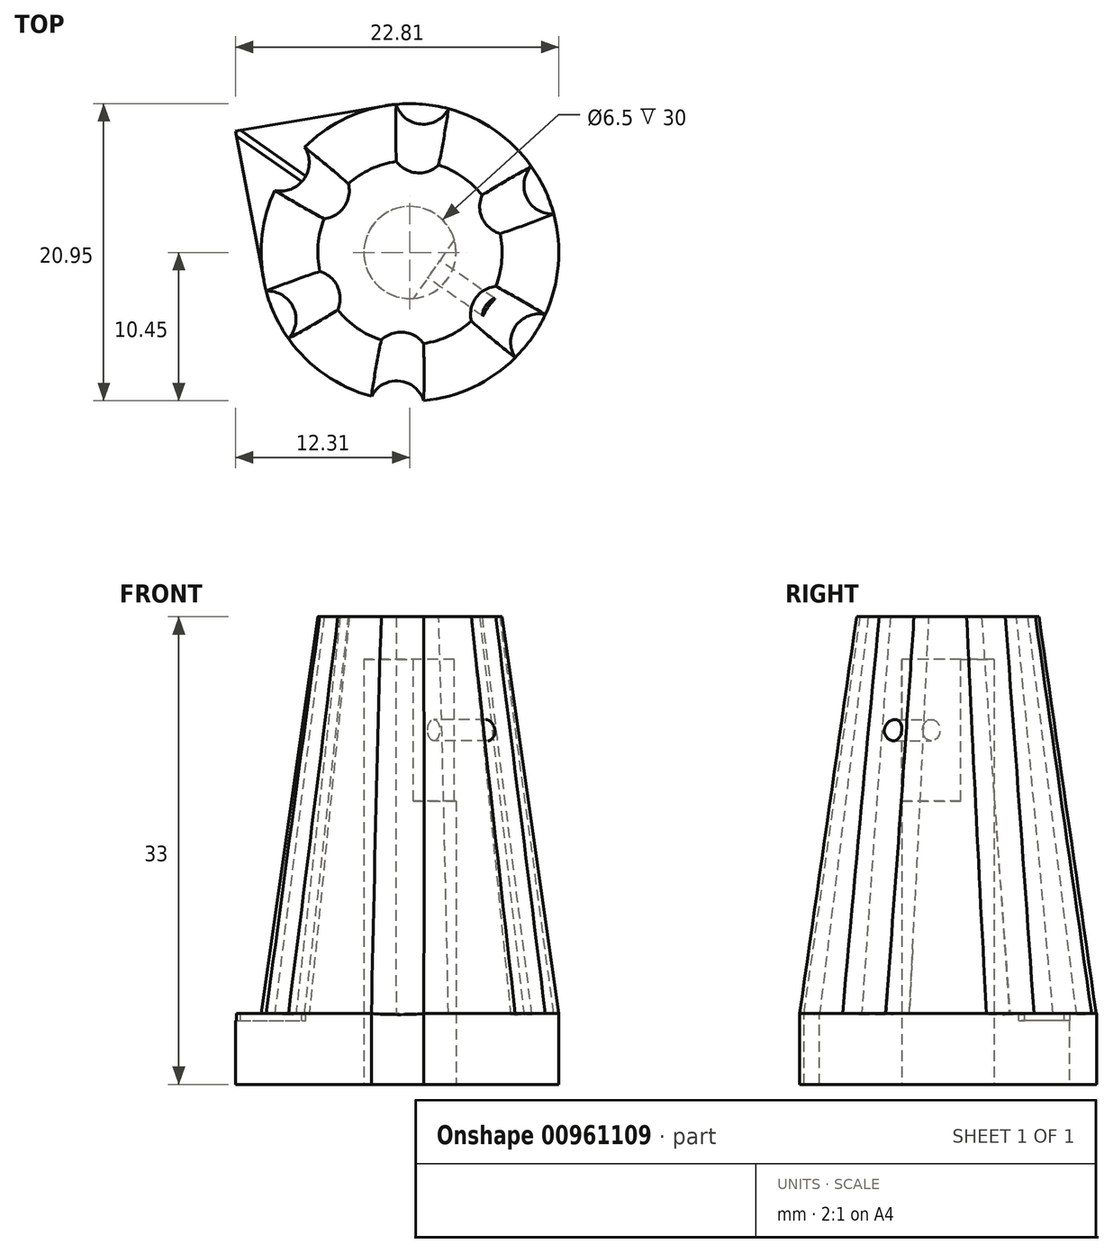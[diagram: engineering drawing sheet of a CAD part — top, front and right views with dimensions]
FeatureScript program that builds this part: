
annotation { "Feature Type Name" : "Feature", "Feature Type Description" : "" }
export const myFeature = defineFeature(function(context is Context, id is Id, definition is map)
    precondition{}
    {
        {
            var Q0;
            Q0=qCreatedBy(makeId("Top.planeOp"),FACE);
            var sketch = newSketch(context, id + "F0", { "sketchPlane" : qUnion([Q0])});
            skCircle(sketch, "E0", {"center": v(0, 0) * mm, "radius": 10.5 * mm});
            skCircle(sketch, "E1", {"center": v(0, 0) * mm, "radius": 3.25 * mm});
            skSolve(sketch);
        }
        {
            var Q0;
            Q0 = qSketchRegion(id + "F0", true);
            var Q1;
            Q1=makeQuery(id+"F0.imprint","IMPRINT",FACE,{"disambiguationData":[TD([[makeQuery(id+"F0.imprint","IMPRINT",EDGE,{"derivedFrom":sQuery(id+"F0.wireOp",EDGE,"E1")}),1.0]])]});
            extrude(context, id + "F1", {"entities" : qUnion([Q0, Q1]), "depth" : 33 * mm, "offsetDistance" : 25 * mm});
        }
        {
            var Q0;
            Q0=makeQuery(id+"F1.opExtrude","CAP_EDGE",EDGE,{"disambiguationData":[OSD([sQuery(id+"F0.wireOp",EDGE,"E0")])],"isStart":false});
            chamfer(context, id + "F2", {"entities" : qUnion([Q0]), "chamferType" : ChamferType.TWO_OFFSETS, "width1" : 4 * mm, "oppositeDirection" : false, "width2" : 28 * mm});
        }
        {
            var Q0;
            Q0=makeQuery(id+"F0.imprint","IMPRINT",FACE,{"disambiguationData":[TD([[makeQuery(id+"F0.imprint","IMPRINT",EDGE,{"derivedFrom":sQuery(id+"F0.wireOp",EDGE,"E1")}),1.0]])]});
            var Q1;
            Q1=sQuery(id+"F0.wireOp",EDGE,"E1");
            extrude(context, id + "F3", {"entities" : qUnion([Q0]), "operationType" : NewBodyOperationType.REMOVE, "surfaceEntities" : qUnion([Q1]), "depth" : 30 * mm, "offsetDistance" : 25 * mm});
        }
        {
            var Q0;
            Q0=qCreatedBy(makeId("Top.planeOp"),FACE);
            cPlane(context, id + "F4", {"entities" : qUnion([Q0]), "cplaneType" : CPlaneType.OFFSET, "offset" : 5 * mm, "width" : 150 * mm, "height" : 150 * mm});
        }
        {
            var Q0;
            Q0=qCreatedBy(id+"F4.planeOp",FACE);
            var sketch = newSketch(context, id + "F5", { "sketchPlane" : qUnion([Q0])});
            skArc(sketch, "E2", {"start": v(0.98, -10.45) * mm, "mid": v(-0.76, -9.06) * mm, "end": v(-2.71, -10.14) * mm});
            skArc(sketch, "E3", {"start": v(-2.71, -10.14) * mm, "mid": v(-0.88, -10.46) * mm, "end": v(0.98, -10.45) * mm});
            skLineSegment(sketch, "E4", {"start": v(-2.71, -10.14) * mm, "end": v(0.98, -10.45) * mm, "construction": true});
            skSolve(sketch);
        }
        {
            var Q0;
            Q0 = qSketchRegion(id + "F5", true);
            extrude(context, id + "F6", {"entities" : qUnion([Q0]), "endBound" : BoundingType.SYMMETRIC, "depth" : 60 * mm, "offsetDistance" : 25 * mm});
        }
        {
            var Q0;
            Q0=makeQuery(id+"F6.opExtrude","SWEPT_BODY",BODY,{"disambiguationData":[OSD([sQuery(id+"F5.wireOp",EDGE,"E2"),sQuery(id+"F5.wireOp",EDGE,"E3")])]});
            var Q1;
            Q1=sQuery(id+"F5.wireOp",EDGE,"E4");
            transform(context, id + "F7", {"entities" : qUnion([Q0]), "transformType" : TransformType.ROTATION, "transformAxis" : qUnion([Q1]), "angle" : 7 * degree, "oppositeDirection" : true, "makeCopy" : false});
        }
        {
            var Q0;
            Q0 = qSketchRegion(id + "F5", true);
            extrude(context, id + "F8", {"entities" : qUnion([Q0]), "operationType" : NewBodyOperationType.REMOVE, "oppositeDirection" : true, "depth" : 25 * mm, "offsetDistance" : 25 * mm});
        }
        {
            var Q0;
            Q0=makeQuery(id+"F6.opExtrude","SWEPT_BODY",BODY,{"disambiguationData":[OSD([sQuery(id+"F5.wireOp",EDGE,"E2"),sQuery(id+"F5.wireOp",EDGE,"E3")])]});
            var Q1;
            Q1=makeQuery(id+"F2.opChamfer","BLEND_FACE",FACE,{"disambiguationData":[OSD([sQuery(id+"F0.wireOp",EDGE,"E0")])]});
            circularPattern(context, id + "F9", {"operationType" : NewBodyOperationType.REMOVE, "entities" : qUnion([Q0]), "axis" : qUnion([Q1]), "angle" : 360 * degree, "instanceCount" : 6, "equalSpace" : true});
        }
        {
            var Q0;
            Q0=makeQuery(id+"F0.imprint","IMPRINT",FACE,{"disambiguationData":[TD([[makeQuery(id+"F0.imprint","IMPRINT",EDGE,{"derivedFrom":sQuery(id+"F0.wireOp",EDGE,"E0")}),1.0]])]});
            var sketch = newSketch(context, id + "F10", { "sketchPlane" : qUnion([Q0])});
            skLineSegment(sketch, "E5", {"start": v(-12.31, 8.57) * mm, "end": v(-10.32, -1.96) * mm});
            skLineSegment(sketch, "E6", {"start": v(-12.31, 8.57) * mm, "end": v(-1.75, 10.35) * mm});
            skLineSegment(sketch, "E7", {"start": v(0, 0) * mm, "end": v(-12.31, 8.57) * mm, "construction": true});
            skSolve(sketch);
        }
        {
            var Q0;
            Q0 = qSketchRegion(id + "F10", true);
            var Q1;
            {var subQ0=sQuery(id+"F10.wireOp",EDGE,"E5");Q1=makeQuery(id+"F10.imprint","IMPRINT",FACE,{"disambiguationData":[TD([[makeQuery(id+"F10.imprint","IMPRINT",EDGE,{"derivedFrom":subQ0}),1.0]])]});}
            extrude(context, id + "F11", {"entities" : qUnion([Q0, Q1]), "operationType" : NewBodyOperationType.ADD, "depth" : 5 * mm, "offsetDistance" : 25 * mm});
        }
        {
            var Q0;
            Q0=makeQuery(id+"F11.opExtrude","CAP_FACE",FACE,{"disambiguationData":[OSD([sQuery(id+"F0.wireOp",EDGE,"E0"),sQuery(id+"F10.wireOp",EDGE,"E5"),sQuery(id+"F10.wireOp",EDGE,"E6"),sQuery(id+"F10.wireOp",EDGE,"PTIv0W1z-BJXX-ulv2-YcXK-IeR1GZzofkEr")])],"isStart":false});
            var sketch = newSketch(context, id + "F12", { "sketchPlane" : qUnion([Q0])});
            skLineSegment(sketch, "E8", {"start": v(-12.31, 8.57) * mm, "end": v(0, 0) * mm, "construction": true});
            skLineSegment(sketch, "E9", {"start": v(-11.96, 8.63) * mm, "end": v(-7.33, 5.4) * mm});
            skLineSegment(sketch, "E10", {"start": v(-12.25, 8.22) * mm, "end": v(-7.62, 5) * mm});
            skSolve(sketch);
        }
        {
            var Q0;
            {var subQ4=sQuery(id+"F12.wireOp",EDGE,"E9");Q0=makeQuery(id+"F12.imprint","IMPRINT",FACE,{"disambiguationData":[TD([[makeQuery(id+"F12.imprint","IMPRINT",EDGE,{"derivedFrom":subQ4}),-1.0]])]});}
            extrude(context, id + "F13", {"entities" : qUnion([Q0]), "operationType" : NewBodyOperationType.REMOVE, "endBound" : BoundingType.SYMMETRIC, "oppositeDirection" : true, "depth" : 1 * mm, "offsetDistance" : 25 * mm});
        }
        {
            var Q0;
            Q0=makeQuery(id+"F3.boolean.opBoolean","COPY",FACE,{"derivedFrom":makeQuery(id+"F3.opExtrude","CAP_FACE",FACE,{"disambiguationData":[OSD([sQuery(id+"F0.wireOp",EDGE,"E1")])],"isStart":false})});
            var sketch = newSketch(context, id + "F14", { "sketchPlane" : qUnion([Q0])});
            skLineSegment(sketch, "E11", {"start": v(0, 0) * mm, "end": v(2.67, 1.86) * mm, "construction": true});
            skLineSegment(sketch, "E12", {"start": v(3.12, -0.9) * mm, "end": v(0.24, 3.24) * mm});
            skSolve(sketch);
        }
        {
            var Q0;
            {var subQ0=sQuery(id+"F14.wireOp",EDGE,"E12");Q0=makeQuery(id+"F14.imprint","IMPRINT",FACE,{"disambiguationData":[TD([[makeQuery(id+"F14.imprint","IMPRINT",EDGE,{"derivedFrom":subQ0}),-1.0]])]});}
            extrude(context, id + "F15", {"entities" : qUnion([Q0]), "operationType" : NewBodyOperationType.ADD, "depth" : 10 * mm, "offsetDistance" : 25 * mm});
        }
        {
            var Q0;
            Q0=makeQuery(id+"F15.opExtrude","SWEPT_FACE",FACE,{"disambiguationData":[OSD([sQuery(id+"F14.wireOp",EDGE,"E12")])]});
            var sketch = newSketch(context, id + "F16", { "sketchPlane" : qUnion([Q0])});
            skCircle(sketch, "E13", {"center": v(0, 25) * mm, "radius": 0.75 * mm});
            skLineSegment(sketch, "E14.bottom", {"start": v(-2.52, 30) * mm, "end": v(2.52, 30) * mm, "construction": true});
            skLineSegment(sketch, "E14.top", {"start": v(-2.52, 20) * mm, "end": v(2.52, 20) * mm, "construction": true});
            skLineSegment(sketch, "E14.left", {"start": v(-2.52, 30) * mm, "end": v(-2.52, 20) * mm, "construction": true});
            skLineSegment(sketch, "E14.right", {"start": v(2.52, 30) * mm, "end": v(2.52, 20) * mm, "construction": true});
            skLineSegment(sketch, "E15", {"start": v(0, 30) * mm, "end": v(0, 20) * mm, "construction": true});
            skSolve(sketch);
        }
        {
            var Q0;
            Q0 = qSketchRegion(id + "F16", true);
            extrude(context, id + "F17", {"entities" : qUnion([Q0]), "operationType" : NewBodyOperationType.REMOVE, "oppositeDirection" : true, "depth" : 25 * mm, "offsetDistance" : 25 * mm});
        }
    });
